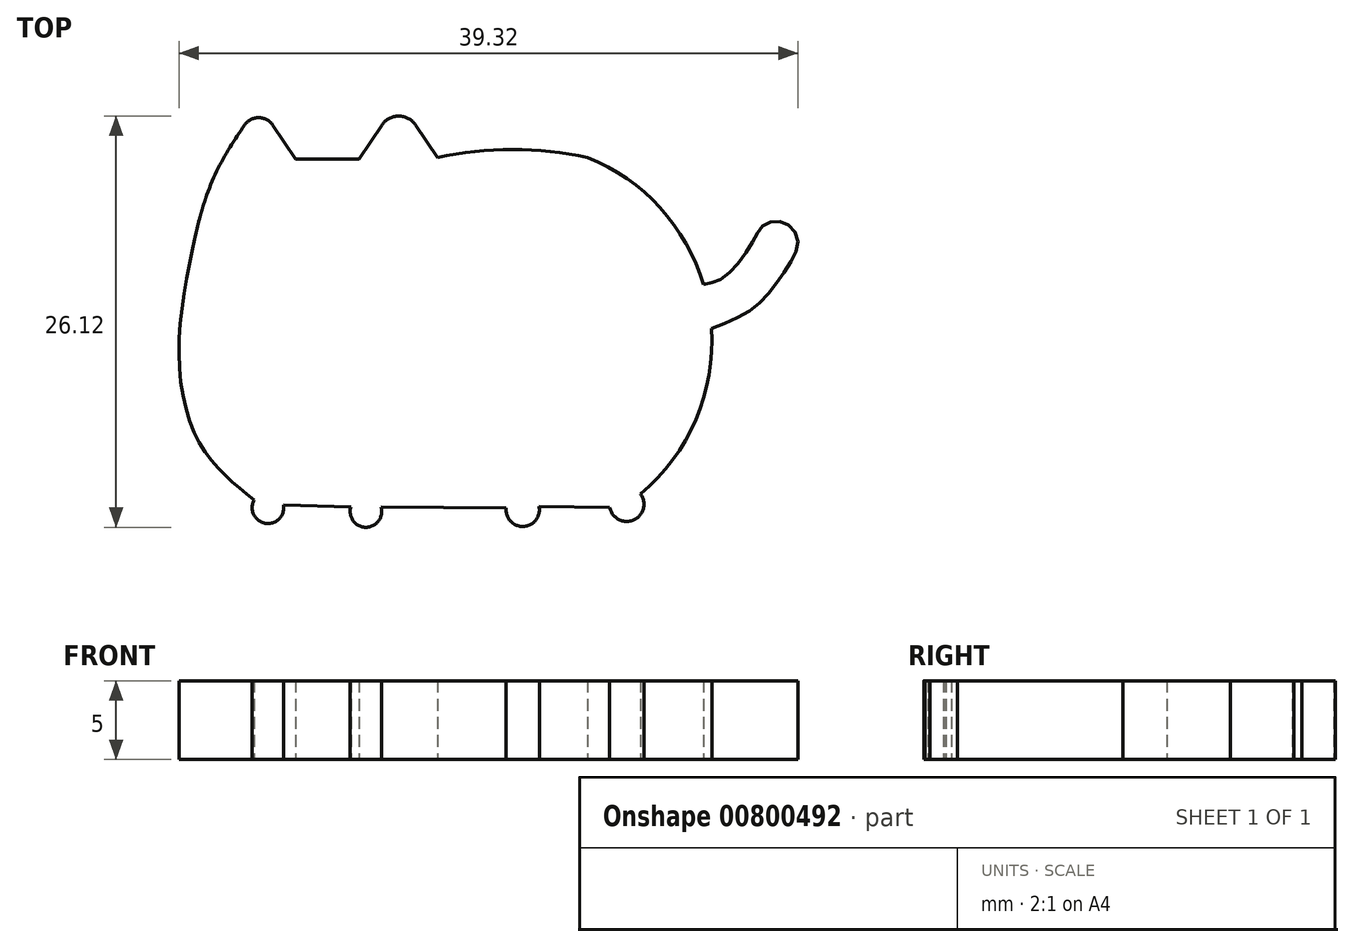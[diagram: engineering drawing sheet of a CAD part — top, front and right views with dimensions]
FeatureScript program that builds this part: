
annotation { "Feature Type Name" : "Feature", "Feature Type Description" : "" }
export const myFeature = defineFeature(function(context is Context, id is Id, definition is map)
    precondition{}
    {
        {
            var Q0;
            Q0=qCreatedBy(makeId("Top.planeOp"),FACE);
            var sketch = newSketch(context, id + "F0", { "sketchPlane" : qUnion([Q0])});
            skArc(sketch, "E0", {"start": v(-18.1, -18.13) * mm, "mid": v(-17.4, -19.6) * mm, "end": v(-16.23, -18.45) * mm});
            skArc(sketch, "E1", {"start": v(-11.95, -18.56) * mm, "mid": v(-11, -19.86) * mm, "end": v(-10.03, -18.58) * mm});
            skArc(sketch, "E2", {"start": v(-2.09, -18.64) * mm, "mid": v(-0.99, -19.81) * mm, "end": v(0, -18.54) * mm});
            skArc(sketch, "E3", {"start": v(4.49, -18.59) * mm, "mid": v(6, -19.4) * mm, "end": v(6.44, -17.75) * mm});
            skArc(sketch, "E4", {"start": v(6.44, -17.75) * mm, "mid": v(9.96, -13.03) * mm, "end": v(10.95, -7.22) * mm});
            skArc(sketch, "E5", {"start": v(3.09, 3.63) * mm, "mid": v(-1.68, 4.14) * mm, "end": v(-6.45, 3.63) * mm});
            skLineSegment(sketch, "E6", {"start": v(-6.45, 3.63) * mm, "end": v(-7.84, 5.7) * mm});
            skArc(sketch, "E7", {"start": v(-7.84, 5.7) * mm, "mid": v(-8.91, 6.26) * mm, "end": v(-9.98, 5.7) * mm});
            skLineSegment(sketch, "E8", {"start": v(-9.98, 5.7) * mm, "end": v(-11.43, 3.54) * mm});
            skLineSegment(sketch, "E9", {"start": v(-11.43, 3.54) * mm, "end": v(-15.45, 3.54) * mm});
            skLineSegment(sketch, "E10", {"start": v(-15.45, 3.54) * mm, "end": v(-16.91, 5.7) * mm});
            skArc(sketch, "E11", {"start": v(-16.91, 5.7) * mm, "mid": v(-17.8, 6.16) * mm, "end": v(-18.7, 5.7) * mm});
            skFitSpline(sketch, "E12", {"points": [v(-18.7, 5.7) * mm, v(-20.72, 2.21) * mm, v(-22.2, -3.1) * mm, v(-22.86, -9.3) * mm, v(-21.82, -14.01) * mm, v(-20.01, -16.48) * mm, v(-18.1, -18.13) * mm], "startDerivative": vector(-13.57, -19.93) * mm, "endDerivative": vector(15.2, -12.11) * mm});
            skLineSegment(sketch, "E13", {"start": v(-16.23, -18.45) * mm, "end": v(-11.95, -18.56) * mm});
            skLineSegment(sketch, "E14", {"start": v(-10.03, -18.58) * mm, "end": v(-2.09, -18.64) * mm});
            skLineSegment(sketch, "E15", {"start": v(0, -18.54) * mm, "end": v(4.49, -18.59) * mm});
            skFitSpline(sketch, "E16", {"points": [v(10.45, -4.44) * mm, v(11.73, -3.98) * mm, v(13.43, -1.95) * mm, v(14.3, -0.64) * mm, v(15.63, -0.53) * mm, v(16.45, -1.73) * mm, v(15.57, -3.65) * mm, v(13.76, -5.84) * mm, v(10.95, -7.22) * mm], "startDerivative": vector(12.43, 2.17) * mm, "endDerivative": vector(-19.61, -7.17) * mm});
            skFitSpline(sketch, "E17", {"points": [v(-21.1, 1.25) * mm, v(-23.57, 1.71) * mm, v(-25.18, 1.67) * mm, v(-25.47, 1.44) * mm, v(-25.41, 1.19) * mm, v(-24.38, 0.94) * mm, v(-22.9, 0.8) * mm, v(-21.37, 0.42) * mm], "startDerivative": vector(-11.81, 2.67) * mm, "endDerivative": vector(9.27, -2.29) * mm});
            skFitSpline(sketch, "E18", {"points": [v(-21.53, -0.16) * mm, v(-23.6, -0.23) * mm, v(-25.33, -0.77) * mm, v(-25.62, -1.4) * mm, v(-25, -1.78) * mm, v(-23.72, -1.37) * mm, v(-21.81, -1.25) * mm], "startDerivative": vector(-9.9, 0.7) * mm, "endDerivative": vector(10.2, -0.4) * mm});
            skArc(sketch, "E19.trimOffspring", {"start": v(10.45, -4.44) * mm, "mid": v(7.69, 0.43) * mm, "end": v(3.09, 3.63) * mm});
            skSolve(sketch);
        }
        {
            var Q0;
            Q0=makeQuery(id+"F0.imprint","IMPRINT",FACE,{"disambiguationData":[TD([[makeQuery(id+"F0.imprint","IMPRINT",EDGE,{"derivedFrom":sQuery(id+"F0.wireOp",EDGE,"E0")}),1.0]])]});
            extrude(context, id + "F1", {"entities" : qUnion([Q0]), "depth" : 5 * mm, "offsetDistance" : 25 * mm});
        }
    });
